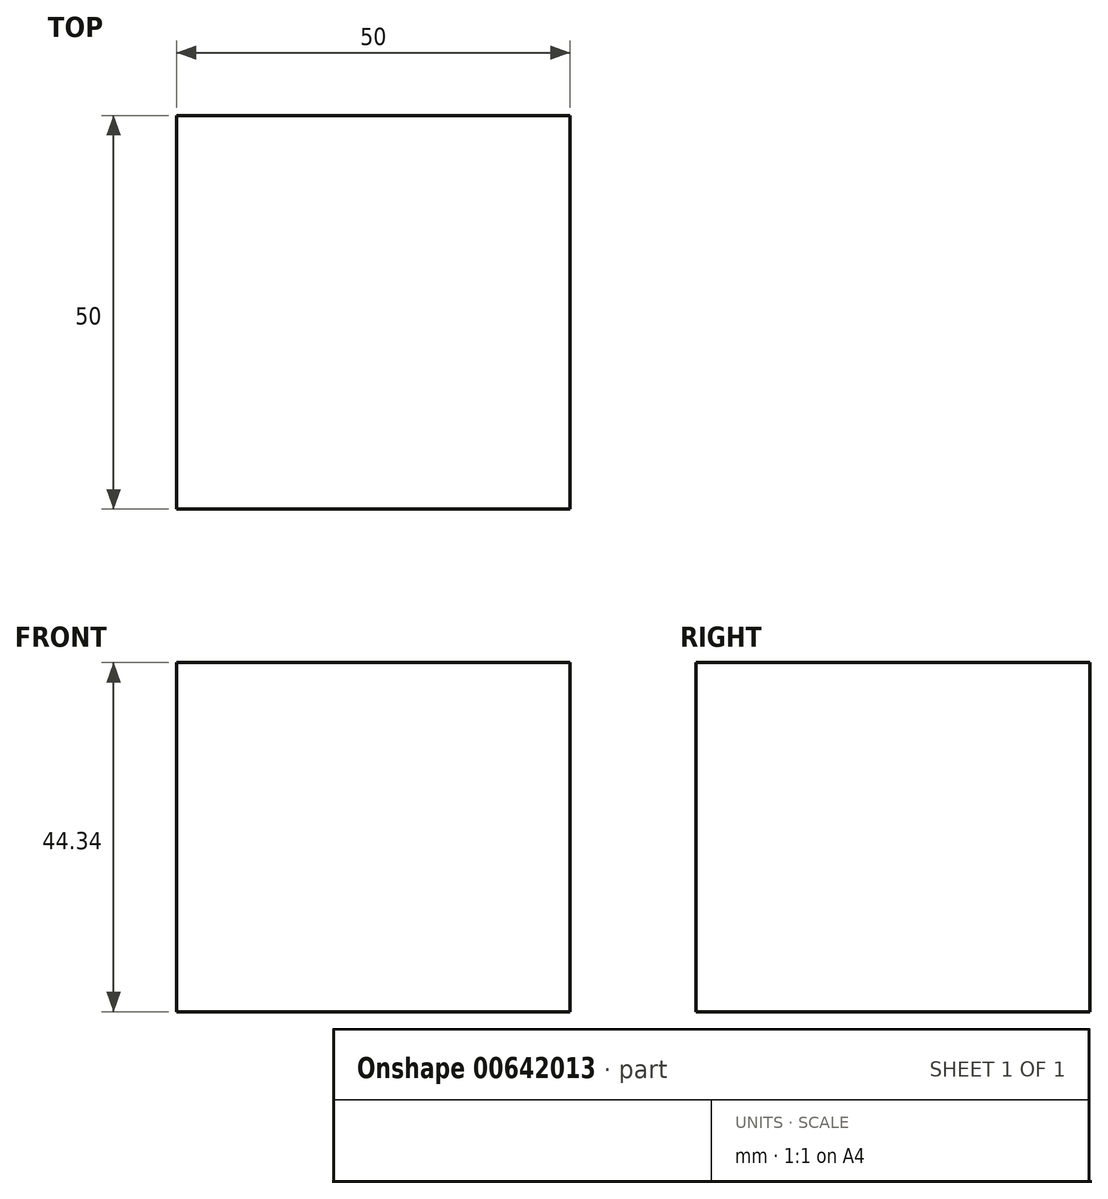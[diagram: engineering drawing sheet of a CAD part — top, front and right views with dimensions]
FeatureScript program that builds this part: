
annotation { "Feature Type Name" : "Feature", "Feature Type Description" : "" }
export const myFeature = defineFeature(function(context is Context, id is Id, definition is map)
    precondition{}
    {
        {
            var Q0;
            Q0=qCreatedBy(makeId("Top.planeOp"),FACE);
            var sketch = newSketch(context, id + "F0", { "sketchPlane" : qUnion([Q0])});
            skLineSegment(sketch, "E0.bottom", {"start": v(25, -25) * mm, "end": v(-25, -25) * mm});
            skLineSegment(sketch, "E0.top", {"start": v(25, 25) * mm, "end": v(-25, 25) * mm});
            skLineSegment(sketch, "E0.left", {"start": v(25, -25) * mm, "end": v(25, 25) * mm});
            skLineSegment(sketch, "E0.right", {"start": v(-25, -25) * mm, "end": v(-25, 25) * mm});
            skPoint(sketch, "E0.middle", {"position": v(0, 0) * mm});
            skSolve(sketch);
        }
        {
            var Q0;
            Q0=makeQuery(id+"F0.imprint","IMPRINT",FACE,{"disambiguationData":[TD([[makeQuery(id+"F0.imprint","IMPRINT",EDGE,{"derivedFrom":sQuery(id+"F0.wireOp",EDGE,"E0.bottom")}),-1.0]])]});
            extrude(context, id + "F1", {"entities" : qUnion([Q0]), "depth" : 44.34 * mm, "offsetDistance" : 25 * mm});
        }
    });
